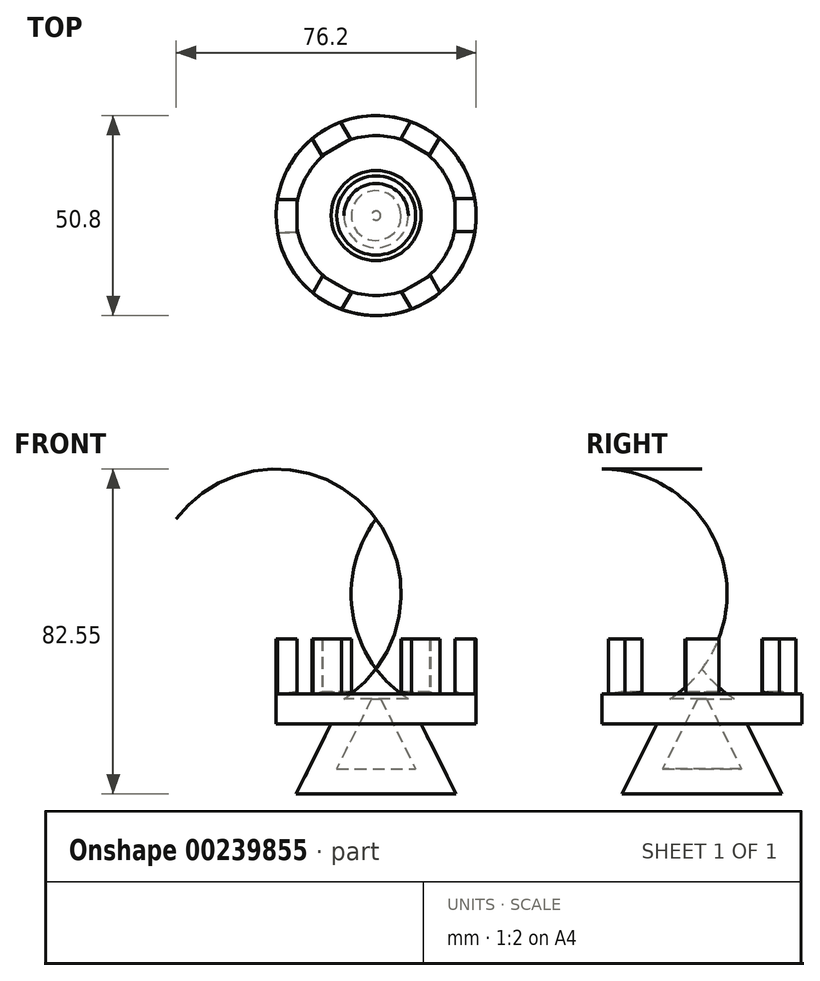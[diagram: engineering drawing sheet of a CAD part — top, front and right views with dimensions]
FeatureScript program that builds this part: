
annotation { "Feature Type Name" : "Feature", "Feature Type Description" : "" }
export const myFeature = defineFeature(function(context is Context, id is Id, definition is map)
    precondition{}
    {
        {
            var Q0;
            Q0=qCreatedBy(makeId("Front.planeOp"),FACE);
            var sketch = newSketch(context, id + "F0", { "sketchPlane" : qUnion([Q0])});
            skLineSegment(sketch, "E0", {"start": v(0, 0) * mm, "end": v(-20.32, 0) * mm});
            skLineSegment(sketch, "E1", {"start": v(-20.32, 0) * mm, "end": v(-11.43, 17.78) * mm});
            skLineSegment(sketch, "E2", {"start": v(-11.43, 17.78) * mm, "end": v(-25.4, 17.78) * mm});
            skLineSegment(sketch, "E3", {"start": v(-25.4, 17.78) * mm, "end": v(-25.4, 25.4) * mm});
            skLineSegment(sketch, "E4", {"start": v(0, 0) * mm, "end": v(0, 50.8) * mm});
            skArc(sketch, "E5", {"start": v(-25.4, 25.4) * mm, "mid": v(-7.44, 32.84) * mm, "end": v(0, 50.8) * mm});
            skSolve(sketch);
        }
        {
            var Q0;
            Q0=makeQuery(id+"F0.imprint","IMPRINT",FACE,{"disambiguationData":[TD([[makeQuery(id+"F0.imprint","IMPRINT",EDGE,{"derivedFrom":sQuery(id+"F0.wireOp",EDGE,"E0")}),-1.0]])]});
            var Q1;
            Q1=sQuery(id+"F0.wireOp",EDGE,"E4");
            revolve(context, id + "F1", {"entities" : qUnion([Q0]), "axis" : qUnion([Q1]), "revolveType" : RevolveType.FULL});
        }
        {
            var Q0;
            Q0=makeQuery(id+"F1.opRevolve","SWEPT_FACE",FACE,{"disambiguationData":[OSD([sQuery(id+"F0.wireOp",EDGE,"E2")])]});
            var sketch = newSketch(context, id + "F2", { "sketchPlane" : qUnion([Q0])});
            skLineSegment(sketch, "E6.bottom", {"start": v(-30.5, 4.3) * mm, "end": v(-20.1, 4.3) * mm});
            skLineSegment(sketch, "E6.top", {"start": v(-30.5, -4.1) * mm, "end": v(-20.1, -4.1) * mm});
            skLineSegment(sketch, "E6.left", {"start": v(-30.5, 4.3) * mm, "end": v(-30.5, -4.1) * mm});
            skLineSegment(sketch, "E6.right", {"start": v(-20.1, 4.3) * mm, "end": v(-20.1, -4.1) * mm});
            skSolve(sketch);
        }
        {
            var Q0;
            {var subQ0=sQuery(id+"F2.wireOp",EDGE,"E6.right");Q0=makeQuery(id+"F2.imprint","IMPRINT",FACE,{"disambiguationData":[TD([[makeQuery(id+"F2.imprint","IMPRINT",EDGE,{"derivedFrom":subQ0}),-1.0]])]});}
            extrude(context, id + "F3", {"entities" : qUnion([Q0]), "operationType" : NewBodyOperationType.ADD, "oppositeDirection" : true, "depth" : 21.59 * mm});
        }
        {
            var Q0;
            Q0=qCreatedBy(makeId("Right.planeOp"),FACE);
            var sketch = newSketch(context, id + "F4", { "sketchPlane" : qUnion([Q0])});
            skLineSegment(sketch, "E7", {"start": v(0, 0) * mm, "end": v(0, 79.47) * mm, "construction": true});
            skSolve(sketch);
        }
        {
            var Q0;
            Q0=makeQuery(id+"F1.opRevolve","SWEPT_BODY",BODY,{"disambiguationData":[OSD([sQuery(id+"F0.wireOp",EDGE,"E0"),sQuery(id+"F0.wireOp",EDGE,"E1"),sQuery(id+"F0.wireOp",EDGE,"E2"),sQuery(id+"F0.wireOp",EDGE,"E3"),sQuery(id+"F0.wireOp",EDGE,"E4"),sQuery(id+"F0.wireOp",EDGE,"E5")])]});
            var Q1;
            Q1=sQuery(id+"F4.wireOp",EDGE,"E7");
            circularPattern(context, id + "F5", {"entities" : qUnion([Q0]), "axis" : qUnion([Q1]), "angle" : 360 * degree, "instanceCount" : 6, "equalSpace" : true});
        }
        {
            var Q0;
            Q0=makeQuery(id+"F1.opRevolve","SWEPT_FACE",FACE,{"disambiguationData":[OSD([sQuery(id+"F0.wireOp",EDGE,"E0")])]});
            var Q1;
            Q1=makeQuery(id+"F1.opRevolve","SWEPT_BODY",BODY,{"disambiguationData":[OSD([sQuery(id+"F0.wireOp",EDGE,"E0"),sQuery(id+"F0.wireOp",EDGE,"E1"),sQuery(id+"F0.wireOp",EDGE,"E2"),sQuery(id+"F0.wireOp",EDGE,"E3"),sQuery(id+"F0.wireOp",EDGE,"E4"),sQuery(id+"F0.wireOp",EDGE,"E5")])]});
            shell(context, id + "F6", {"isHollow" : true, "entities" : qUnion([Q0]), "parts" : qUnion([Q1]), "thickness" : 6.35 * mm});
        }
    });
